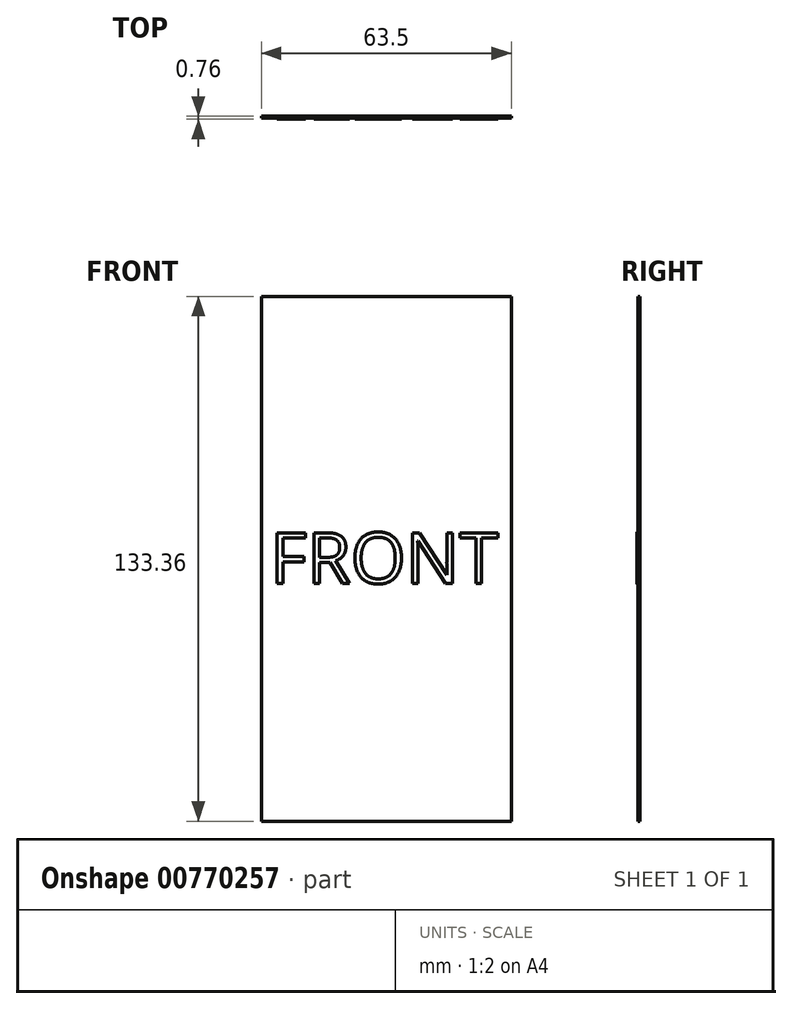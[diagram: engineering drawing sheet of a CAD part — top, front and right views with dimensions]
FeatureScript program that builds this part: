
annotation { "Feature Type Name" : "Feature", "Feature Type Description" : "" }
export const myFeature = defineFeature(function(context is Context, id is Id, definition is map)
    precondition{}
    {
        {
            var Q0;
            Q0=qCreatedBy(makeId("Front.planeOp"),FACE);
            var sketch = newSketch(context, id + "F0", { "sketchPlane" : qUnion([Q0])});
            skLineSegment(sketch, "E0.bottom", {"start": v(31.75, -66.68) * mm, "end": v(-31.75, -66.68) * mm});
            skLineSegment(sketch, "E0.top", {"start": v(31.75, 66.68) * mm, "end": v(-31.75, 66.68) * mm});
            skLineSegment(sketch, "E0.left", {"start": v(31.75, -66.68) * mm, "end": v(31.75, 66.67) * mm});
            skLineSegment(sketch, "E0.right", {"start": v(-31.75, -66.68) * mm, "end": v(-31.75, 66.67) * mm});
            skPoint(sketch, "E0.middle", {"position": v(0, 0) * mm});
            skSolve(sketch);
        }
        {
            var Q0;
            Q0=qSketchRegion(id+"F0",true);
            extrude(context, id + "F1", {"entities" : qUnion([Q0]), "endBound" : BoundingType.SYMMETRIC, "depth" : 0.5 * mm});
        }
        {
            var Q0;
            Q0=makeQuery(id+"F1.opExtrude","CAP_FACE",FACE,{"disambiguationData":[OSD([sQuery(id+"F0.wireOp",EDGE,"E0.bottom"),sQuery(id+"F0.wireOp",EDGE,"E0.top"),sQuery(id+"F0.wireOp",EDGE,"E0.left"),sQuery(id+"F0.wireOp",EDGE,"E0.right")])],"isStart":false});
            var sketch = newSketch(context, id + "F2", { "sketchPlane" : qUnion([Q0])});
            skText(sketch, "E1", { "text": "FRONT", "fontName": "OpenSans-Regular.ttf"});
            const initialGuessF2  = {"E1": [-0.02947, -0.00624, 1, 0, 0.01296]};
            skSetInitialGuess(sketch, initialGuessF2);
            skSolve(sketch);
        }
        {
            var Q0;
            Q0=qSketchRegion(id+"F2",true);
            extrude(context, id + "F3", {"entities" : qUnion([Q0]), "operationType" : NewBodyOperationType.ADD, "depth" : 0.25 * mm});
        }
    });
